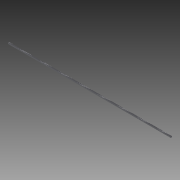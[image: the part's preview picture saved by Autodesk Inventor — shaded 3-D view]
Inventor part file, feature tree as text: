
AUTODESK INVENTOR PART (.ipt)
format: ipt  version: 2013 (Build 170138000, 138)  size: 3,601,408 bytes
history: native  units: in
note: dims shown in document units (in); Inventor stores cm internally (conversion verified against a paired STEP export)
features: extrude x2, sketch x2, pattern_linear x1
ambient origin geometry x8: Origin, YZ Plane, XZ Plane, XY Plane, X Axis, Y Axis, Z Axis, Center Point
bodies: Solid1 (feature_tree)
feature tree (5):
  extrude  "Extrusion1"  Depth=0.5in
  extrude  "Extrusion2"  Depth=0.05in
  pattern_linear  "Rectangular Pattern2"  Spacing1=0.7559in  [1 undecoded]
  sketch  "Sketch1"  dims[d0=0.5in d1=0.5in]
  sketch  "Sketch2"  dims[d3=0.0in d8=0.05in d9=0.7559in d10=0.7559in d11=72.0in d12=0.0in d17=0.0167in d18=0.0333in d19=0.035in d20=566.9291in d22=0.05in]
note: 1 required parameter value undecoded (feature->parameter linkage not recoverable at this tier; creation-order binding heuristic only, values carry confidence <= 0.55)
